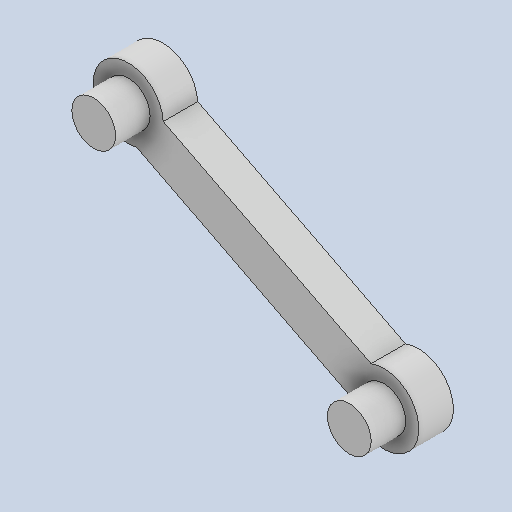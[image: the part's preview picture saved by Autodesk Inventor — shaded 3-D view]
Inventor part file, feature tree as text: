
AUTODESK INVENTOR PART (.ipt)
format: ipt  version: 2022 (Build 260153000, 153)  size: 115,200 bytes
history: native  units: in
note: dims shown in document units (in); Inventor stores cm internally (conversion verified against a paired STEP export)
features: other x3, sketch x1
ambient origin geometry x8: Origin, YZ Plane, XZ Plane, XY Plane, X Axis, Y Axis, Z Axis, Center Point
bodies: Solid1 (feature_tree)
feature tree (4):
  other  "Component25.ipt"
  other  "Solid2::Component25.ipt"
  other  "TaggingFeature1"
  sketch  "Sketch2"  dims[d0=0.3937in]
